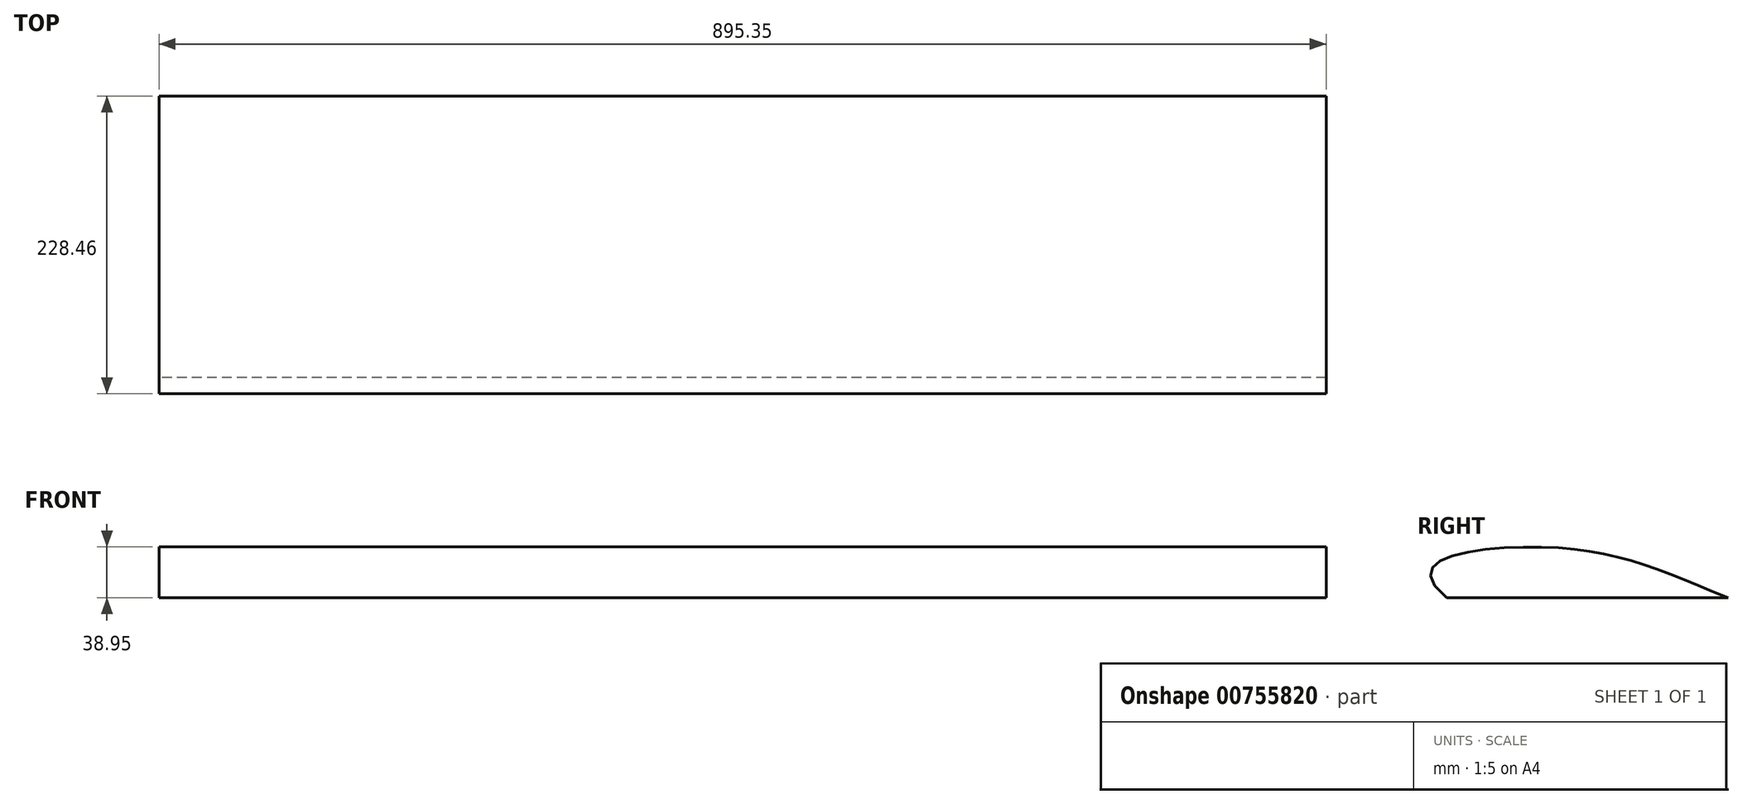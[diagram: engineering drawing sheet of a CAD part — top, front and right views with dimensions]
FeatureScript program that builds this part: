
annotation { "Feature Type Name" : "Feature", "Feature Type Description" : "" }
export const myFeature = defineFeature(function(context is Context, id is Id, definition is map)
    precondition{}
    {
        {
            var Q0;
            Q0=qCreatedBy(makeId("Right.planeOp"),FACE);
            var sketch = newSketch(context, id + "F0", { "sketchPlane" : qUnion([Q0])});
            skLineSegment(sketch, "E0", {"start": v(-215.9, 0) * mm, "end": v(0, 0) * mm});
            skFitSpline(sketch, "E1", {"points": [v(-215.9, 0) * mm, v(-150.55, 38.95) * mm, v(0, 0) * mm], "startDerivative": vector(-283.75, 226.93) * mm, "endDerivative": vector(284.4, -113.5) * mm});
            skSolve(sketch);
        }
        {
            var Q0;
            Q0=makeQuery(id+"F0.imprint","IMPRINT",FACE,{"disambiguationData":[TD([[makeQuery(id+"F0.imprint","IMPRINT",EDGE,{"derivedFrom":sQuery(id+"F0.wireOp",EDGE,"E0")}),1.0]])]});
            extrude(context, id + "F1", {"entities" : qUnion([Q0]), "depth" : 895.35 * mm, "offsetDistance" : 25.4 * mm});
        }
    });
